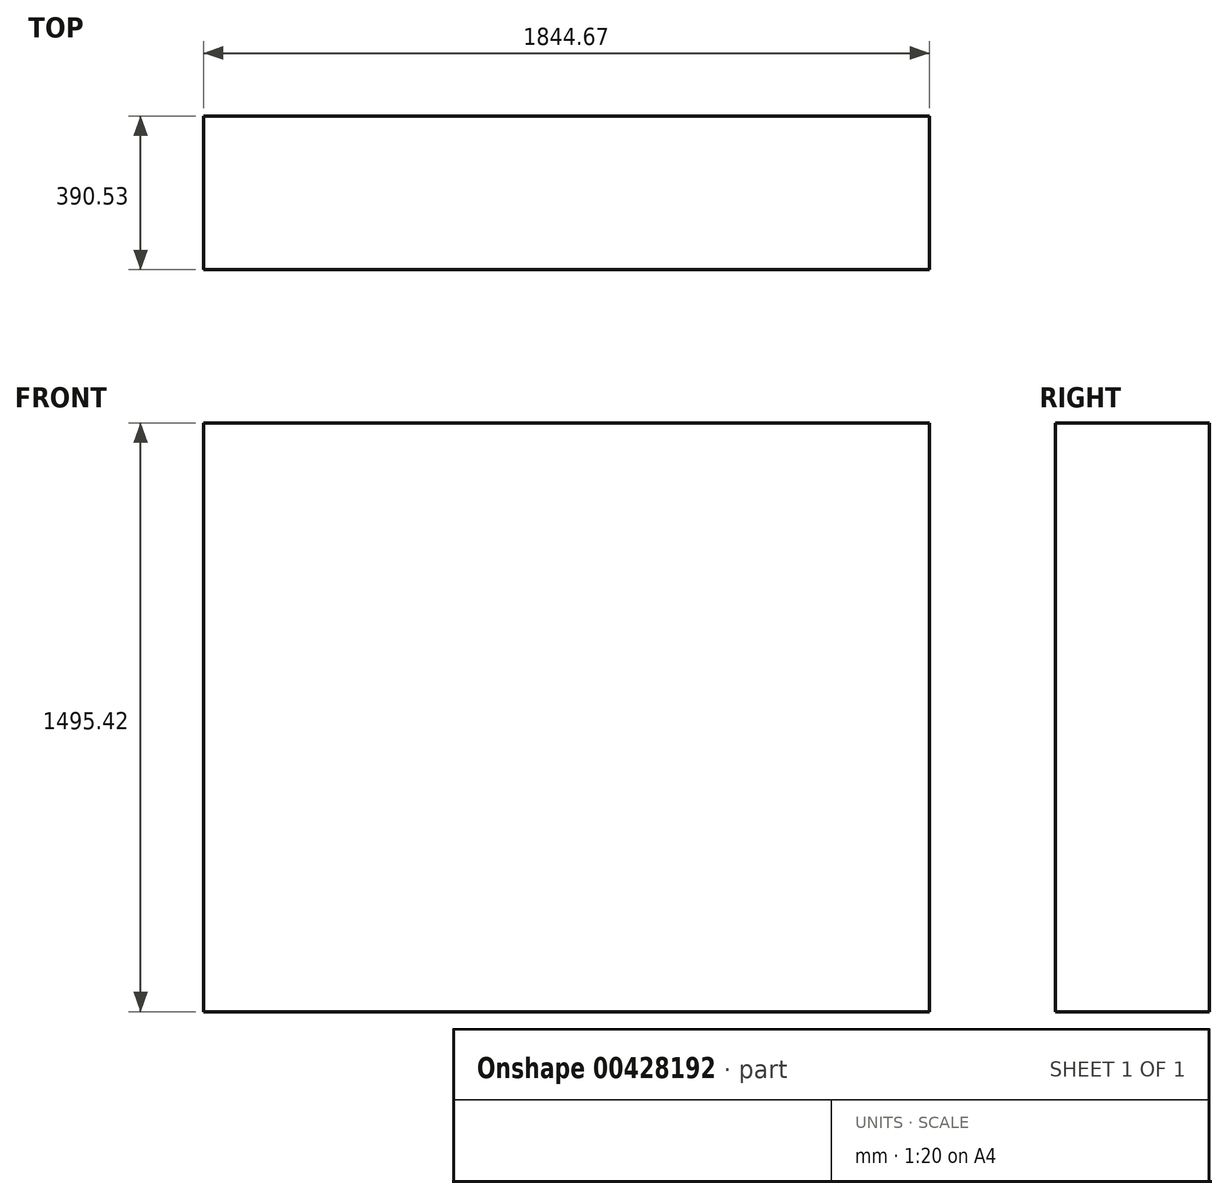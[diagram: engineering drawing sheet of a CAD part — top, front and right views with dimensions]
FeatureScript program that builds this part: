
annotation { "Feature Type Name" : "Feature", "Feature Type Description" : "" }
export const myFeature = defineFeature(function(context is Context, id is Id, definition is map)
    precondition{}
    {
        {
            var Q0;
            Q0=qCreatedBy(makeId("Front.planeOp"),FACE);
            var sketch = newSketch(context, id + "F0", { "sketchPlane" : qUnion([Q0])});
            skLineSegment(sketch, "E0.bottom", {"start": v(0, 0) * mm, "end": v(1844.67, 0) * mm});
            skLineSegment(sketch, "E0.top", {"start": v(0, 1495.42) * mm, "end": v(1844.67, 1495.42) * mm});
            skLineSegment(sketch, "E0.left", {"start": v(0, 0) * mm, "end": v(0, 1495.42) * mm});
            skLineSegment(sketch, "E0.right", {"start": v(1844.67, 0) * mm, "end": v(1844.67, 1495.42) * mm});
            skSolve(sketch);
        }
        {
            var Q0;
            Q0=makeQuery(id+"F0.imprint","IMPRINT",FACE,{"disambiguationData":[TD([[makeQuery(id+"F0.imprint","IMPRINT",EDGE,{"derivedFrom":sQuery(id+"F0.wireOp",EDGE,"E0.bottom")}),1.0]])]});
            extrude(context, id + "F1", {"entities" : qUnion([Q0]), "depth" : 390.52 * mm});
        }
    });
